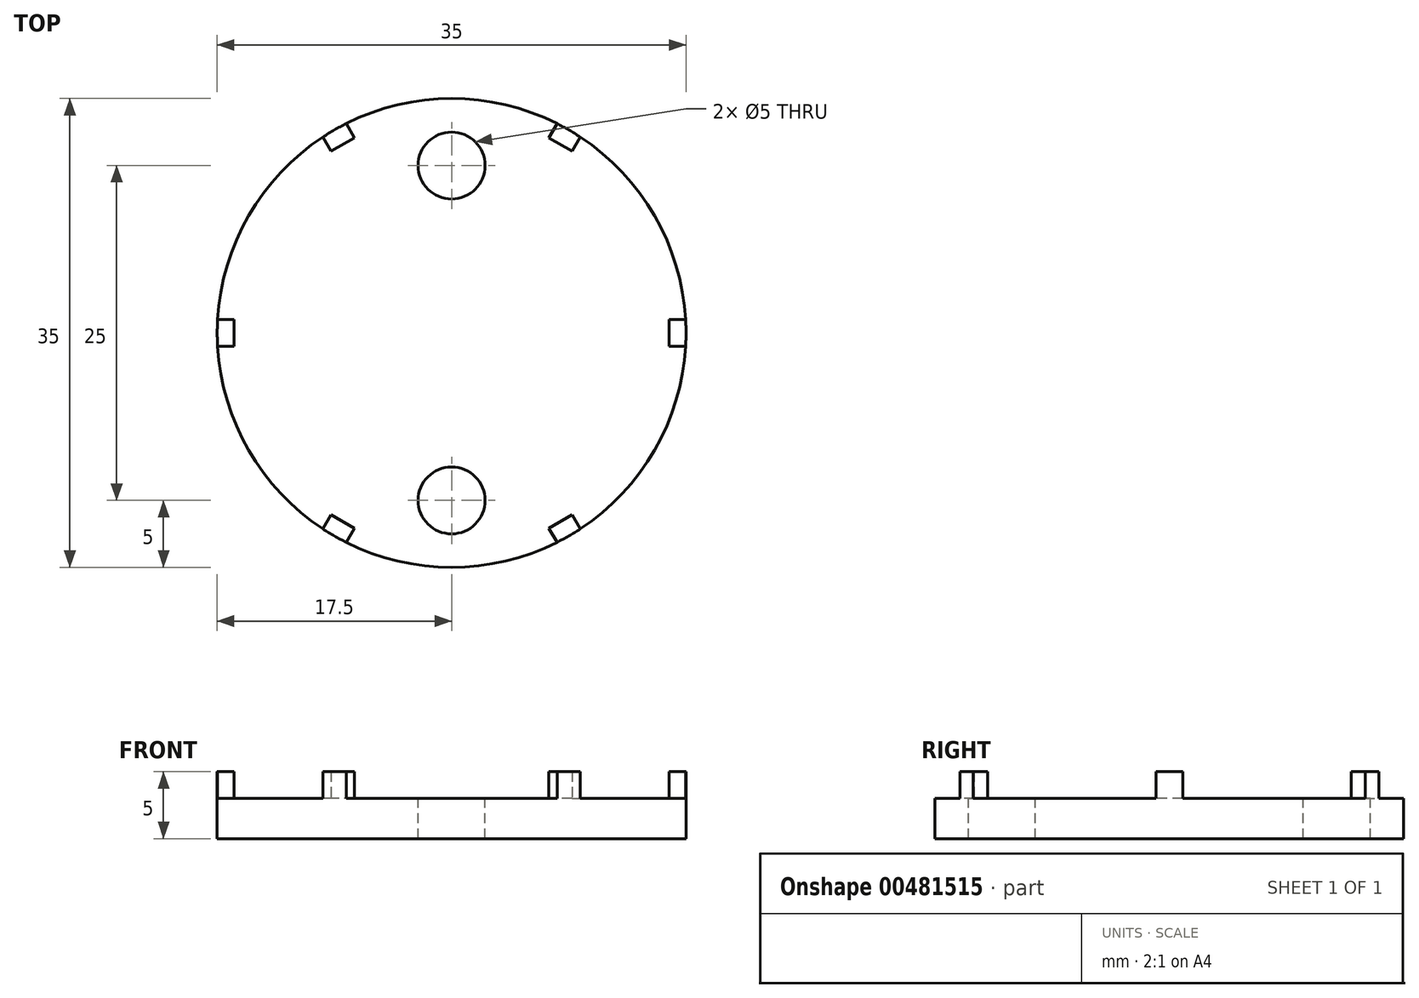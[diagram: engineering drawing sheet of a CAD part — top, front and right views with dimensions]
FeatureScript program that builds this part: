
annotation { "Feature Type Name" : "Feature", "Feature Type Description" : "" }
export const myFeature = defineFeature(function(context is Context, id is Id, definition is map)
    precondition{}
    {
        {
            var Q0;
            Q0=qCreatedBy(makeId("Top.planeOp"),FACE);
            var sketch = newSketch(context, id + "F0", { "sketchPlane" : qUnion([Q0])});
            skCircle(sketch, "E0", {"center": v(0, 0) * mm, "radius": 17.5 * mm});
            skLineSegment(sketch, "E1.left", {"start": v(-17.48, 0.8) * mm, "end": v(-17.48, 0.76) * mm});
            skLineSegment(sketch, "E1.right", {"start": v(-14.74, 0.8) * mm, "end": v(-14.74, 0.76) * mm});
            skLineSegment(sketch, "E2.bottom", {"start": v(-16.25, 1) * mm, "end": v(-17.5, 1) * mm});
            skLineSegment(sketch, "E2.top", {"start": v(-16.25, -1) * mm, "end": v(-17.5, -1) * mm});
            skLineSegment(sketch, "E2.left", {"start": v(-16.25, 1) * mm, "end": v(-16.25, -1) * mm});
            skLineSegment(sketch, "E2.right", {"start": v(-17.5, 1) * mm, "end": v(-17.5, -1) * mm});
            skPoint(sketch, "E2.middle", {"position": v(-16.88, 0) * mm});
            skPoint(sketch, "E3", {"position": v(-17.5, 0) * mm});
            skCircle(sketch, "E4", {"center": v(0, -12.5) * mm, "radius": 2.5 * mm});
            skCircle(sketch, "E5", {"center": v(0, 0) * mm, "radius": 12.5 * mm, "construction": true});
            skCircle(sketch, "E6", {"center": v(0, 12.5) * mm, "radius": 2.5 * mm});
            skSolve(sketch);
        }
        {
            var Q0;
            Q0=qCreatedBy(makeId("Right.planeOp"),FACE);
            var sketch = newSketch(context, id + "F1", { "sketchPlane" : qUnion([Q0])});
            skLineSegment(sketch, "E7", {"start": v(0, -40) * mm, "end": v(0, 40) * mm});
            skSolve(sketch);
        }
        {
            var Q0;
            {var subQ0=sQuery(id+"F0.wireOp",EDGE,"E2.left");Q0=makeQuery(id+"F0.imprint","IMPRINT",FACE,{"disambiguationData":[TD([[makeQuery(id+"F0.imprint","IMPRINT",EDGE,{"derivedFrom":subQ0}),-1.0]])]});}
            extrude(context, id + "F2", {"entities" : qUnion([Q0]), "depth" : 2 * mm});
        }
        {
            var Q0;
            {var subQ5=sQuery(id+"F0.wireOp",EDGE,"E2.left");Q0=makeQuery(id+"F0.imprint","IMPRINT",FACE,{"disambiguationData":[TD([[makeQuery(id+"F0.imprint","IMPRINT",EDGE,{"derivedFrom":subQ5}),1.0]])]});}
            var Q1;
            {var subQ0=sQuery(id+"F0.wireOp",EDGE,"E2.left");Q1=makeQuery(id+"F0.imprint","IMPRINT",FACE,{"disambiguationData":[TD([[makeQuery(id+"F0.imprint","IMPRINT",EDGE,{"derivedFrom":subQ0}),-1.0]])]});}
            extrude(context, id + "F3", {"entities" : qUnion([Q0, Q1]), "operationType" : NewBodyOperationType.ADD, "oppositeDirection" : true, "depth" : 3 * mm});
        }
        {
            var Q0;
            Q0=makeQuery(id+"F2.opExtrude","SWEPT_BODY",BODY,{"disambiguationData":[OSD([sQuery(id+"F0.wireOp",EDGE,"E0"),sQuery(id+"F0.wireOp",EDGE,"E2.bottom"),sQuery(id+"F0.wireOp",EDGE,"E2.top"),sQuery(id+"F0.wireOp",EDGE,"E2.left")])]});
            var Q1;
            Q1=sQuery(id+"F1.wireOp",EDGE,"E7");
            circularPattern(context, id + "F4", {"operationType" : NewBodyOperationType.ADD, "entities" : qUnion([Q0]), "axis" : qUnion([Q1]), "angle" : 360 * degree, "instanceCount" : 6, "equalSpace" : true});
        }
        {
            var Q0;
            Q0=makeQuery(id+"F0.imprint","IMPRINT",FACE,{"disambiguationData":[TD([[makeQuery(id+"F0.imprint","IMPRINT",EDGE,{"derivedFrom":sQuery(id+"F0.wireOp",EDGE,"E4")}),1.0]])]});
            var Q1;
            Q1=makeQuery(id+"F0.imprint","IMPRINT",FACE,{"disambiguationData":[TD([[makeQuery(id+"F0.imprint","IMPRINT",EDGE,{"derivedFrom":sQuery(id+"F0.wireOp",EDGE,"E6")}),1.0]])]});
            var Q2;
            Q2=sQuery(id+"F0.wireOp",EDGE,"E5");
            var Q3;
            Q3=sQuery(id+"F0.wireOp",EDGE,"E4");
            var Q4;
            {var subQ0=makeQuery(id+"F3.opExtrude","CAP_FACE",FACE,{"disambiguationData":[OSD([sQuery(id+"F0.wireOp",EDGE,"E0"),sQuery(id+"F0.wireOp",EDGE,"E4")])],"isStart":false});Q4=makeQuery(id+"F4.boolean.opBoolean","MERGE",FACE,{"derivedFrom":[subQ0,makeQuery(id+"F4.opPattern","COPY",FACE,{"derivedFrom":subQ0,"instanceName":"1"}),makeQuery(id+"F4.opPattern","COPY",FACE,{"derivedFrom":subQ0,"instanceName":"2"}),makeQuery(id+"F4.opPattern","COPY",FACE,{"derivedFrom":subQ0,"instanceName":"3"}),makeQuery(id+"F4.opPattern","COPY",FACE,{"derivedFrom":subQ0,"instanceName":"4"}),makeQuery(id+"F4.opPattern","COPY",FACE,{"derivedFrom":subQ0,"instanceName":"5"})]});}
            extrude(context, id + "F5", {"entities" : qUnion([Q0, Q1]), "operationType" : NewBodyOperationType.REMOVE, "surfaceEntities" : qUnion([Q2, Q3]), "endBound" : BoundingType.UP_TO_NEXT, "oppositeDirection" : true, "endBoundEntityFace" : qUnion([Q4]), "depth" : 25 * mm});
        }
    });
